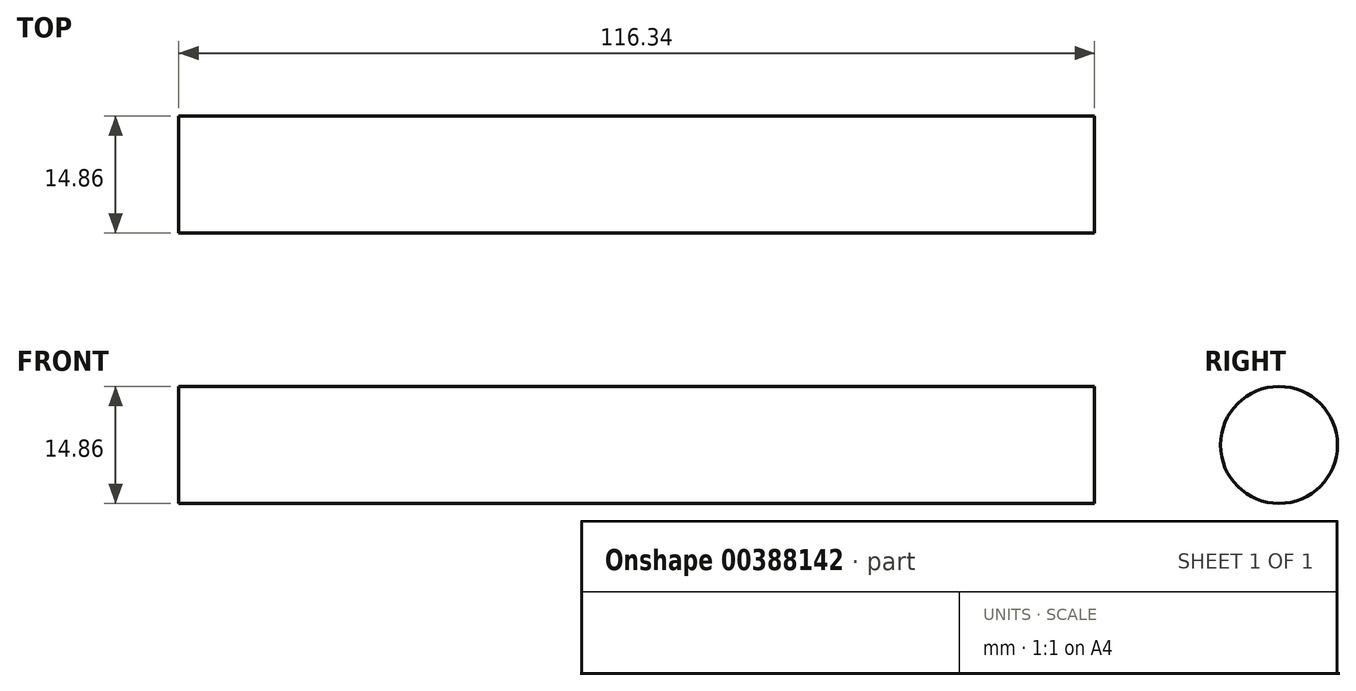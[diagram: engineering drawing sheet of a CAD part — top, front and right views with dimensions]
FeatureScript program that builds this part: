
annotation { "Feature Type Name" : "Feature", "Feature Type Description" : "" }
export const myFeature = defineFeature(function(context is Context, id is Id, definition is map)
    precondition{}
    {
        {
            var Q0;
            Q0=qCreatedBy(makeId("Right.planeOp"),FACE);
            var sketch = newSketch(context, id + "F0", { "sketchPlane" : qUnion([Q0])});
            skCircle(sketch, "E0", {"center": v(0, 0) * mm, "radius": 7.43 * mm});
            skSolve(sketch);
        }
        {
            var Q0;
            Q0=makeQuery(id+"F0.imprint","IMPRINT",FACE,{"disambiguationData":[TD([[makeQuery(id+"F0.imprint","IMPRINT",EDGE,{"derivedFrom":sQuery(id+"F0.wireOp",EDGE,"E0")}),1.0]])]});
            extrude(context, id + "F1", {"entities" : qUnion([Q0]), "endBound" : BoundingType.SYMMETRIC, "depth" : 116.33 * mm});
        }
    });
